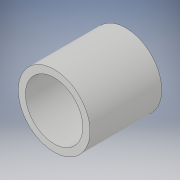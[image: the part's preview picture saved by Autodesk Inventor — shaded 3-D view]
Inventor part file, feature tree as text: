
AUTODESK INVENTOR PART (.ipt)
format: ipt  version: 2019 (Build 230136000, 136)  size: 101,376 bytes
history: native  units: mm
features: extrude x2, sketch x2
ambient origin geometry x8: Origin, YZ Plane, XZ Plane, XY Plane, X Axis, Y Axis, Z Axis, Center Point
bodies: Solid1 (feature_tree)
feature tree (4):
  extrude  "Extrusion1"  Depth=250.0mm TaperAngle=0.0deg
  extrude  "Extrusion2"  Depth=21.5mm TaperAngle=0.0deg
  sketch  "Sketch1"  dims[d0=250.0mm d1=250.0mm d2=0.0mm]
  sketch  "Sketch2"  dims[d3=200.0mm d4=21.5mm d5=0.0mm]
